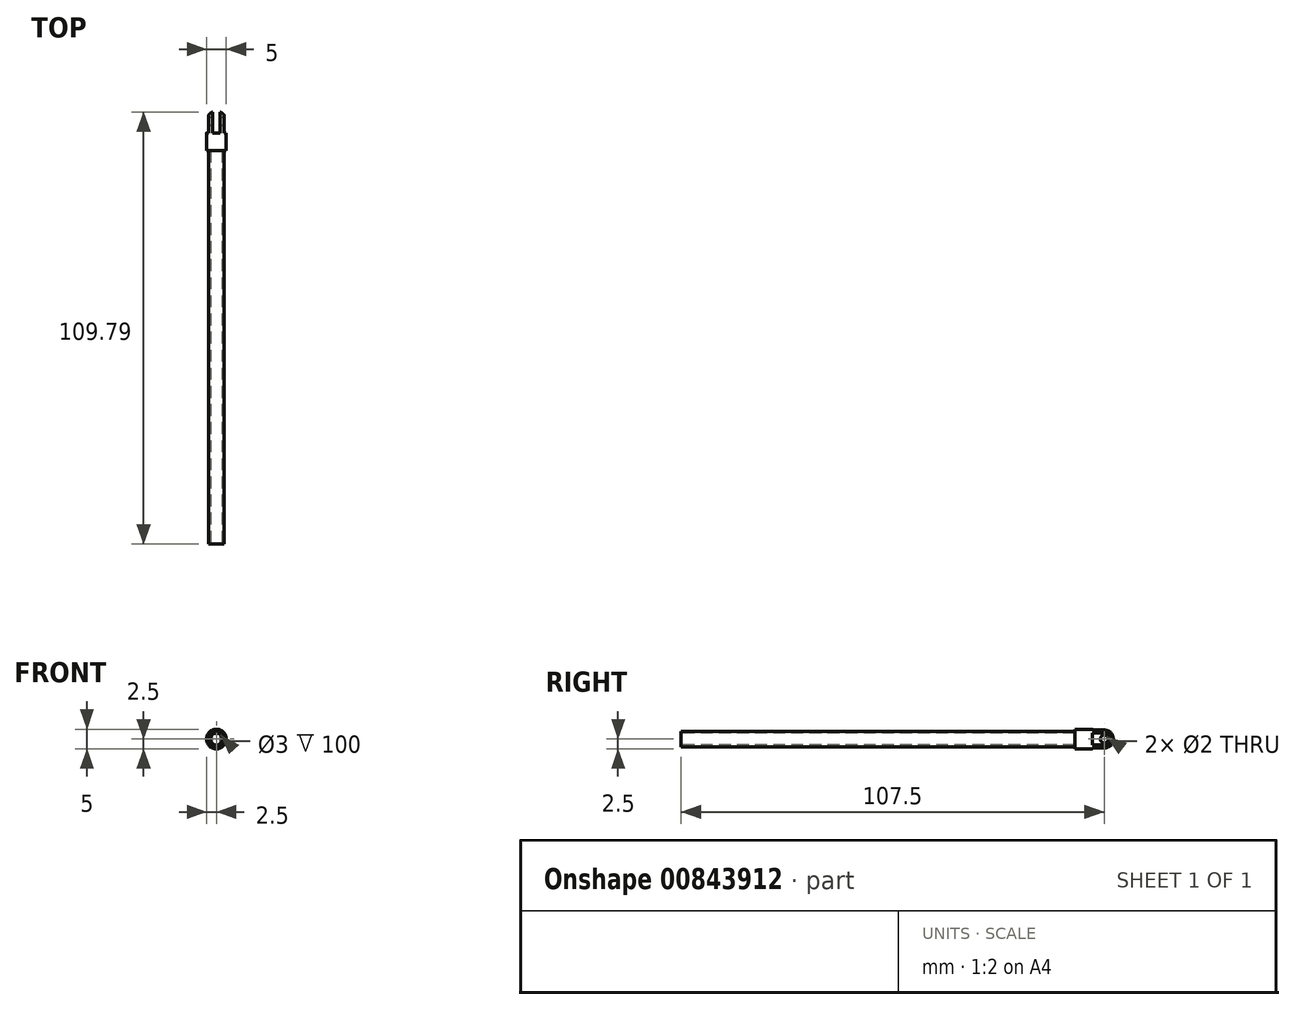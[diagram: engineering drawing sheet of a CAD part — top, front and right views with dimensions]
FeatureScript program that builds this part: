
annotation { "Feature Type Name" : "Feature", "Feature Type Description" : "" }
export const myFeature = defineFeature(function(context is Context, id is Id, definition is map)
    precondition{}
    {
        {
            var Q0;
            Q0=qCreatedBy(makeId("Front.planeOp"),FACE);
            var sketch = newSketch(context, id + "F0", { "sketchPlane" : qUnion([Q0])});
            skCircle(sketch, "E0", {"center": v(0, 0) * mm, "radius": 2 * mm});
            skSolve(sketch);
        }
        {
            var Q0;
            Q0 = qSketchRegion(id + "F0", true);
            extrude(context, id + "F1", {"entities" : qUnion([Q0]), "endBound" : BoundingType.SYMMETRIC, "depth" : 100 * mm, "offsetDistance" : 25 * mm});
        }
        {
            var Q0;
            Q0=makeQuery(id+"F1.opExtrude","CAP_FACE",FACE,{"disambiguationData":[OSD([sQuery(id+"F0.wireOp",EDGE,"E0")])],"isStart":true});
            var sketch = newSketch(context, id + "F2", { "sketchPlane" : qUnion([Q0])});
            skCircle(sketch, "E1", {"center": v(0, 0) * mm, "radius": 2.5 * mm});
            skSolve(sketch);
        }
        {
            var Q0;
            Q0 = qSketchRegion(id + "F2", true);
            extrude(context, id + "F3", {"entities" : qUnion([Q0]), "operationType" : NewBodyOperationType.ADD, "depth" : 7.5 * mm, "offsetDistance" : 25 * mm});
        }
        {
            var Q0;
            Q0=qCreatedBy(makeId("Top.planeOp"),FACE);
            var sketch = newSketch(context, id + "F4", { "sketchPlane" : qUnion([Q0])});
            skArc(sketch, "E2", {"start": v(2.5, 57.5) * mm, "mid": v(1.77, 59.27) * mm, "end": v(0, 60) * mm});
            skLineSegment(sketch, "E3", {"start": v(0, 57.5) * mm, "end": v(0, 60) * mm});
            skLineSegment(sketch, "E4", {"start": v(0, 57.5) * mm, "end": v(2.5, 57.5) * mm});
            skSolve(sketch);
        }
        {
            var Q0;
            Q0=makeQuery(id+"F4.imprint","IMPRINT",FACE,{"disambiguationData":[TD([[makeQuery(id+"F4.imprint","IMPRINT",EDGE,{"derivedFrom":sQuery(id+"F4.wireOp",EDGE,"E2")}),1.0]])]});
            var Q1;
            Q1=sQuery(id+"F4.wireOp",EDGE,"E3");
            revolve(context, id + "F5", {"operationType" : NewBodyOperationType.ADD, "surfaceOperationType" : NewSurfaceOperationType.NEW, "entities" : qUnion([Q0]), "axis" : qUnion([Q1]), "revolveType" : RevolveType.FULL});
        }
        {
            var Q0;
            Q0=qCreatedBy(makeId("Top.planeOp"),FACE);
            var sketch = newSketch(context, id + "F6", { "sketchPlane" : qUnion([Q0])});
            skLineSegment(sketch, "E5.bottom", {"start": v(1, 54.5) * mm, "end": v(-1, 54.5) * mm});
            skLineSegment(sketch, "E5.top", {"start": v(1, 64.97) * mm, "end": v(-1, 64.97) * mm});
            skLineSegment(sketch, "E5.left", {"start": v(1, 54.5) * mm, "end": v(1, 64.97) * mm});
            skLineSegment(sketch, "E5.right", {"start": v(-1, 54.5) * mm, "end": v(-1, 64.97) * mm});
            skPoint(sketch, "E5.middle", {"position": v(0, 59.73) * mm});
            skLineSegment(sketch, "E6.bottom", {"start": v(-2, 54.5) * mm, "end": v(-4.67, 54.5) * mm});
            skLineSegment(sketch, "E6.top", {"start": v(-2, 63.88) * mm, "end": v(-4.67, 63.88) * mm});
            skLineSegment(sketch, "E6.left", {"start": v(-2, 54.5) * mm, "end": v(-2, 63.88) * mm});
            skLineSegment(sketch, "E6.right", {"start": v(-4.67, 54.5) * mm, "end": v(-4.67, 63.88) * mm});
            skPoint(sketch, "E6.middle", {"position": v(-3.34, 59.2) * mm});
            skLineSegment(sketch, "E7.bottom", {"start": v(4.06, 54.5) * mm, "end": v(2, 54.5) * mm});
            skLineSegment(sketch, "E7.top", {"start": v(4.06, 65.73) * mm, "end": v(2, 65.73) * mm});
            skLineSegment(sketch, "E7.left", {"start": v(4.06, 54.5) * mm, "end": v(4.06, 65.73) * mm});
            skLineSegment(sketch, "E7.right", {"start": v(2, 54.5) * mm, "end": v(2, 65.73) * mm});
            skPoint(sketch, "E7.middle", {"position": v(3.03, 60.12) * mm});
            skSolve(sketch);
        }
        {
            var Q0;
            Q0 = qSketchRegion(id + "F6", true);
            extrude(context, id + "F7", {"entities" : qUnion([Q0]), "operationType" : NewBodyOperationType.REMOVE, "endBound" : BoundingType.SYMMETRIC, "oppositeDirection" : true, "depth" : 25 * mm, "offsetDistance" : 25 * mm});
        }
        {
            var Q0;
            Q0=makeQuery(id+"F7.boolean.opBoolean","COPY",FACE,{"derivedFrom":makeQuery(id+"F7.opExtrude","SWEPT_FACE",FACE,{"disambiguationData":[OSD([sQuery(id+"F6.wireOp",EDGE,"E7.right")])]})});
            var sketch = newSketch(context, id + "F8", { "sketchPlane" : qUnion([Q0])});
            skCircle(sketch, "E8", {"center": v(57.5, 0) * mm, "radius": 1 * mm});
            skSolve(sketch);
        }
        {
            var Q0;
            Q0 = qSketchRegion(id + "F8", true);
            extrude(context, id + "F9", {"entities" : qUnion([Q0]), "operationType" : NewBodyOperationType.REMOVE, "endBound" : BoundingType.THROUGH_ALL, "oppositeDirection" : true, "depth" : 25 * mm, "offsetDistance" : 25 * mm});
        }
        {
            var Q0;
            Q0=makeQuery(id+"F1.opExtrude","CAP_FACE",FACE,{"disambiguationData":[OSD([sQuery(id+"F0.wireOp",EDGE,"E0")])],"isStart":false});
            var sketch = newSketch(context, id + "F10", { "sketchPlane" : qUnion([Q0])});
            skCircle(sketch, "E9", {"center": v(0, 0) * mm, "radius": 1.5 * mm});
            skSolve(sketch);
        }
        {
            var Q0;
            Q0 = qSketchRegion(id + "F10", true);
            extrude(context, id + "F11", {"entities" : qUnion([Q0]), "operationType" : NewBodyOperationType.REMOVE, "oppositeDirection" : true, "depth" : 100 * mm, "offsetDistance" : 25 * mm});
        }
    });
